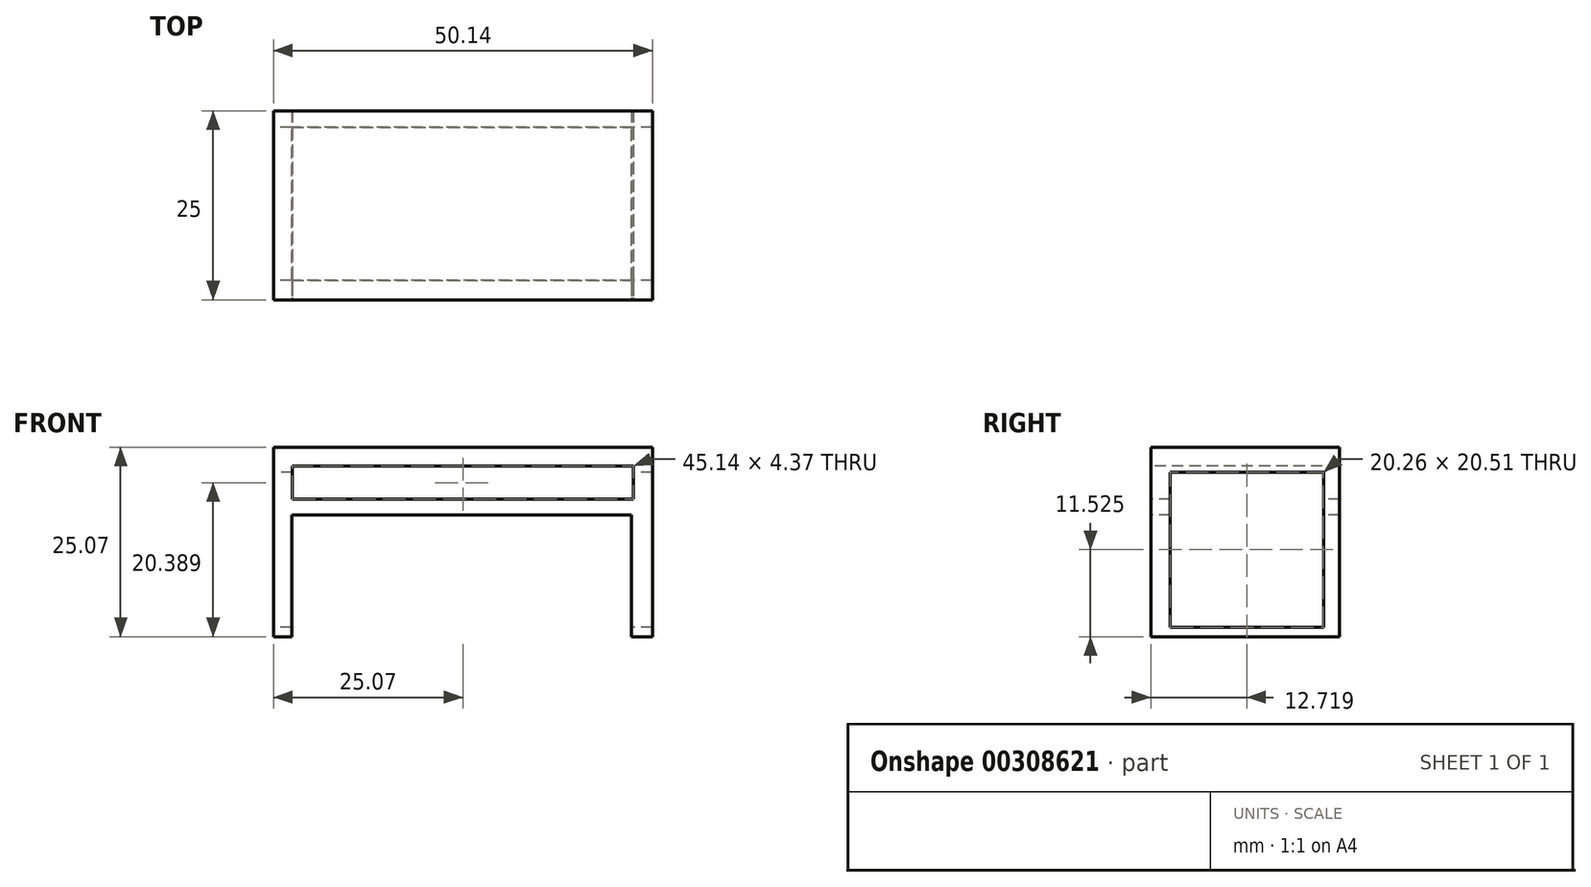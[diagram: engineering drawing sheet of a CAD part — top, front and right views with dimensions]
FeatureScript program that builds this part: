
annotation { "Feature Type Name" : "Feature", "Feature Type Description" : "" }
export const myFeature = defineFeature(function(context is Context, id is Id, definition is map)
    precondition{}
    {
        {
            var Q0;
            Q0=qCreatedBy(makeId("Front.planeOp"),FACE);
            var sketch = newSketch(context, id + "F0", { "sketchPlane" : qUnion([Q0])});
            skLineSegment(sketch, "E0.bottom", {"start": v(-65.84, 56.46) * mm, "end": v(34.44, 56.46) * mm});
            skLineSegment(sketch, "E0.top", {"start": v(-65.84, 6.33) * mm, "end": v(34.44, 6.33) * mm});
            skLineSegment(sketch, "E0.left", {"start": v(-65.84, 56.46) * mm, "end": v(-65.84, 6.33) * mm});
            skLineSegment(sketch, "E0.right", {"start": v(34.44, 56.46) * mm, "end": v(34.44, 6.33) * mm});
            skSolve(sketch);
        }
        {
            var Q0;
            Q0=qSketchRegion(id+"F0",true);
            extrude(context, id + "F1", {"entities" : qUnion([Q0]), "depth" : 50 * mm});
        }
        {
            var Q0;
            Q0=makeQuery(id+"F1.opExtrude","CAP_FACE",FACE,{"disambiguationData":[OSD([sQuery(id+"F0.wireOp",EDGE,"E0.bottom"),sQuery(id+"F0.wireOp",EDGE,"E0.top"),sQuery(id+"F0.wireOp",EDGE,"E0.left"),sQuery(id+"F0.wireOp",EDGE,"E0.right")])],"isStart":false});
            var sketch = newSketch(context, id + "F2", { "sketchPlane" : qUnion([Q0])});
            skLineSegment(sketch, "E1.bottom", {"start": v(-60.84, 51.46) * mm, "end": v(29.44, 51.46) * mm});
            skLineSegment(sketch, "E1.top", {"start": v(-60.84, 42.73) * mm, "end": v(29.44, 42.73) * mm});
            skLineSegment(sketch, "E1.left", {"start": v(-60.84, 51.46) * mm, "end": v(-60.84, 42.73) * mm});
            skLineSegment(sketch, "E1.right", {"start": v(29.44, 51.46) * mm, "end": v(29.44, 42.73) * mm});
            skSolve(sketch);
        }
        {
            var Q0;
            Q0=makeQuery(id+"F2.imprint","IMPRINT",FACE,{"disambiguationData":[TD([[makeQuery(id+"F2.imprint","IMPRINT",EDGE,{"derivedFrom":sQuery(id+"F2.wireOp",EDGE,"E1.bottom")}),-1.0]])]});
            extrude(context, id + "F3", {"entities" : qUnion([Q0]), "operationType" : NewBodyOperationType.REMOVE, "endBound" : BoundingType.THROUGH_ALL, "oppositeDirection" : true, "depth" : 25 * mm});
        }
        {
            var Q0;
            Q0=makeQuery(id+"F1.opExtrude","SWEPT_FACE",FACE,{"disambiguationData":[OSD([sQuery(id+"F0.wireOp",EDGE,"E0.left")])]});
            var sketch = newSketch(context, id + "F4", { "sketchPlane" : qUnion([Q0])});
            skSolve(sketch);
        }
        {
            var Q0;
            {var subQ0=sQuery(id+"F0.wireOp",EDGE,"E0.left");Q0=makeQuery(id+"F4.imprint","IMPRINT",FACE,{"disambiguationData":[TD([[makeQuery(id+"F4.imprint","IMPRINT",EDGE,{"derivedFrom":makeQuery(id+"F1.opExtrude","CAP_EDGE",EDGE,{"disambiguationData":[OSD([subQ0])],"isStart":true})}),1.0]])]});}
            var sketch = newSketch(context, id + "F5", { "sketchPlane" : qUnion([Q0])});
            skLineSegment(sketch, "E2.bottom", {"start": v(4.3, 49.88) * mm, "end": v(44.82, 49.88) * mm});
            skLineSegment(sketch, "E2.top", {"start": v(4.3, 8.86) * mm, "end": v(44.82, 8.86) * mm});
            skLineSegment(sketch, "E2.left", {"start": v(4.3, 49.88) * mm, "end": v(4.3, 8.86) * mm});
            skLineSegment(sketch, "E2.right", {"start": v(44.82, 49.88) * mm, "end": v(44.82, 8.86) * mm});
            skSolve(sketch);
        }
        {
            var Q0;
            Q0=qSketchRegion(id+"F5",true);
            extrude(context, id + "F6", {"entities" : qUnion([Q0]), "operationType" : NewBodyOperationType.REMOVE, "endBound" : BoundingType.THROUGH_ALL, "oppositeDirection" : true, "depth" : 25 * mm});
        }
        {
            var Q0;
            Q0=makeQuery(id+"F1.opExtrude","CAP_FACE",FACE,{"disambiguationData":[OSD([sQuery(id+"F0.wireOp",EDGE,"E0.bottom"),sQuery(id+"F0.wireOp",EDGE,"E0.top"),sQuery(id+"F0.wireOp",EDGE,"E0.left"),sQuery(id+"F0.wireOp",EDGE,"E0.right")])],"isStart":false});
            var sketch = newSketch(context, id + "F7", { "sketchPlane" : qUnion([Q0])});
            skLineSegment(sketch, "E3.bottom", {"start": v(-61.02, 38.49) * mm, "end": v(28.87, 38.49) * mm});
            skLineSegment(sketch, "E3.top", {"start": v(-61.02, 6.33) * mm, "end": v(28.87, 6.33) * mm});
            skLineSegment(sketch, "E3.left", {"start": v(-61.02, 38.49) * mm, "end": v(-61.02, 6.33) * mm});
            skLineSegment(sketch, "E3.right", {"start": v(28.87, 38.49) * mm, "end": v(28.87, 6.33) * mm});
            skSolve(sketch);
        }
        {
            var Q0;
            Q0=qSketchRegion(id+"F7",true);
            extrude(context, id + "F8", {"entities" : qUnion([Q0]), "operationType" : NewBodyOperationType.REMOVE, "endBound" : BoundingType.THROUGH_ALL, "oppositeDirection" : true, "depth" : 25 * mm});
        }
        {
            var Q0;
            Q0=makeQuery(id+"F1.opExtrude","SWEPT_BODY",BODY,{"disambiguationData":[OSD([sQuery(id+"F0.wireOp",EDGE,"E0.bottom"),sQuery(id+"F0.wireOp",EDGE,"E0.top"),sQuery(id+"F0.wireOp",EDGE,"E0.left"),sQuery(id+"F0.wireOp",EDGE,"E0.right")])]});
            var Q1;
            Q1=qCreatedBy(makeId("Origin.pointOp"),VERTEX);
            var Q2;
            Q2=qCreatedBy(makeId("Origin.pointOp"),VERTEX);
            transform(context, id + "F9", {"entities" : qUnion([Q0]), "transformType" : TransformType.SCALE_UNIFORMLY, "scale" : 0.5, "scalePoint" : qUnion([Q2]), "makeCopy" : false});
        }
    });
